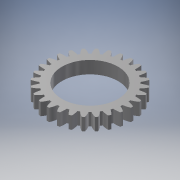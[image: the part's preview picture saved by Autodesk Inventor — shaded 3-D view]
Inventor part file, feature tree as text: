
AUTODESK INVENTOR PART (.ipt)
format: ipt  version: 2018 (Build 220112000, 112)  size: 257,024 bytes
history: native  units: mm (DEFAULTED — no unit token found)
features: plane x3, other x3, sketch x3, extrude x2
ambient origin geometry x8: Origin, YZ Plane, XZ Plane, XY Plane, X Axis, Y Axis, Z Axis, Center Point
bodies: Solid1 (feature_tree)
feature tree (11):
  extrude  "Extrusion1"  Depth=5.0mm TaperAngle=0.0deg
  plane  "Work Plane2"
  plane  "Work Plane8"
  plane  "Work Plane9"
  other  "Engrenage cylindrique"
  extrude  "Extrusion2"  Depth=10.0mm TaperAngle=0.0deg
  sketch  "Sketch1"  dims[d0=33.749074mm d1=5.0mm d2=0.0mm]
  sketch  "Sketch2"  dims[d3=31.438596mm d4=10.0mm d5=0.0mm d16=32.0mm d17=0.0mm d34=1.121997mm d39=0.0mm d41=0.0mm d43=32.0mm d46=32.0mm d47=0.0mm d48=0.0mm d49=22.5mm d50=10.0mm d51=0.0mm]
  other  "Srf1"
  sketch  "Esquisse3"
  other  "Diamètre primitif"
